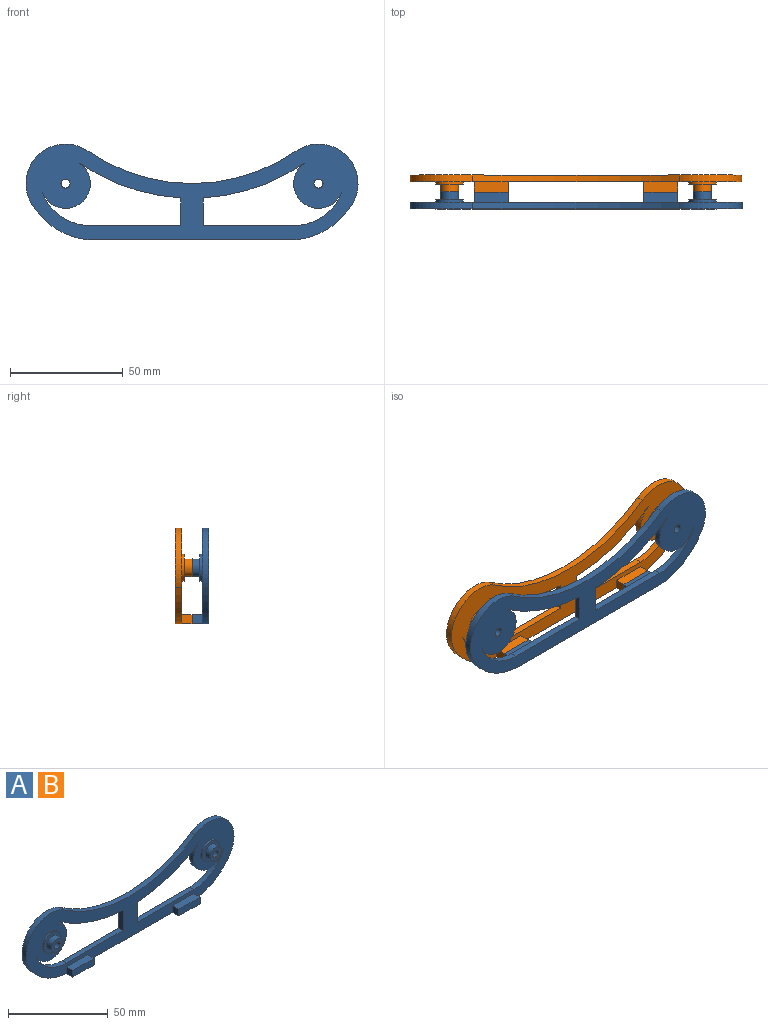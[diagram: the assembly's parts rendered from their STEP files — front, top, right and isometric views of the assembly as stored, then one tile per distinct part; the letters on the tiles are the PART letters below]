
ASSEMBLY  parts=2 mates=1
PART A: 36 faces, bbox 147x7.5x42.5 mm
  f0: plane 147x42.49mm, normal (0,-1,0), area 2621.3mm2, adj f1,f3,f5,f6,f7,f8,f9,f10
  f1: cylinder r=6mm len=12mm, axis (0,1,0), area 37.7mm2, adj f0,f2
  f2: plane 12x12mm, normal (0,-1,0), area 62.8mm2, adj f1,f14
  f3: cylinder r=6mm len=12mm, axis (0,1,0), area 37.7mm2, adj f0,f4
  f4: plane 12x12mm, normal (0,-1,0), area 62.8mm2, adj f3,f11
  f5: cylinder r=80.85mm len=92.07mm, axis (0,1,0), area 293.9mm2, adj f0,f6,f10,f13
  f6: cylinder r=17.5mm len=27.46mm, axis (0,1,0), area 141.8mm2, adj f0,f5,f7,f13
  f7: cylinder r=32.63mm len=26.15mm, axis (0,1,0), area 96.2mm2, adj f0,f6,f8,f13
  f8: plane 90x7.5mm, normal (0,0,-1), area 405mm2, adj f0,f7,f9,f13,f18,f19,f20,f22
  f9: cylinder r=32.63mm len=26.15mm, axis (0,1,0), area 96.2mm2, adj f0,f8,f10,f13
  f10: cylinder r=17.5mm len=27.46mm, axis (0,1,0), area 141.8mm2, adj f0,f5,f9,f13
  f11: cylinder r=4mm len=8mm, axis (0,1,0), area 88mm2, adj f4,f12
  f12: plane 8x8mm, normal (0,-1,0), area 37.7mm2, adj f11,f17
  f13: plane 147x42.49mm, normal (0,1,0), area 2942.3mm2, adj f5,f6,f7,f8,f9,f10,f16,f17
  f14: cylinder r=4mm len=8mm, axis (0,1,0), area 88mm2, adj f2,f15
  f15: plane 8x8mm, normal (0,-1,0), area 37.7mm2, adj f14,f16
  f16: cylinder r=2mm len=7.5mm, axis (0,-1,0), area 94.2mm2, adj f13,f15
  f17: cylinder r=2mm len=7.5mm, axis (0,-1,0), area 94.2mm2, adj f12,f13
  f18: plane 15x4mm, normal (0,-1,0), area 60mm2, adj f8,f19,f20,f21
  f19: plane 4.5x4mm, normal (1,0,0), area 18mm2, adj f0,f8,f18,f21
  f20: plane 4.5x4mm, normal (-1,0,0), area 18mm2, adj f0,f8,f18,f21
  f21: plane 15x4.5mm, normal (0,0,1), area 67.5mm2, adj f0,f18,f19,f20
  f22: plane 15x4mm, normal (0,-1,0), area 60mm2, adj f8,f23,f24,f25
  f23: plane 4.5x4mm, normal (1,0,0), area 18mm2, adj f0,f8,f22,f24
  f24: plane 15x4.5mm, normal (0,0,1), area 67.5mm2, adj f0,f22,f23,f25
  f25: plane 4.5x4mm, normal (-1,0,0), area 18mm2, adj f0,f8,f22,f24
  f26: plane 40x3mm, normal (0,0,1), area 120mm2, adj f0,f13,f27,f30
  f27: cylinder r=22.75mm len=21.3mm, axis (0,-1,0), area 82.7mm2, adj f0,f13,f26,f28
  f28: cylinder r=11mm len=21.3mm, axis (0,-1,0), area 123.6mm2, adj f0,f13,f27,f29
  f29: cylinder r=87.35mm len=44.74mm, axis (0,-1,0), area 143.7mm2, adj f0,f13,f28,f30
  f30: plane 12.26x3mm, normal (1,0,0), area 36.8mm2, adj f0,f13,f26,f29
  f31: plane 40x3mm, normal (0,0,1), area 120mm2, adj f0,f13,f32,f33
  f32: plane 12.26x3mm, normal (-1,0,0), area 36.8mm2, adj f0,f13,f31,f34
  f33: cylinder r=22.75mm len=21.3mm, axis (0,-1,0), area 82.7mm2, adj f0,f13,f31,f35
  f34: cylinder r=87.35mm len=44.74mm, axis (0,-1,0), area 143.7mm2, adj f0,f13,f32,f35
  f35: cylinder r=11mm len=21.3mm, axis (0,-1,0), area 123.6mm2, adj f0,f13,f33,f34
PART B: same geometry as A
PLACE A rot(axis=(0,0,1),180deg) t=(68.83,10.36,-32.68)mm
PLACE B t=(-43.17,25.36,-32.68)mm
MATE parallel A.f22 <-> B.f18  axis (0,1,0) through (-24.67,17.86,-30.68)mm
